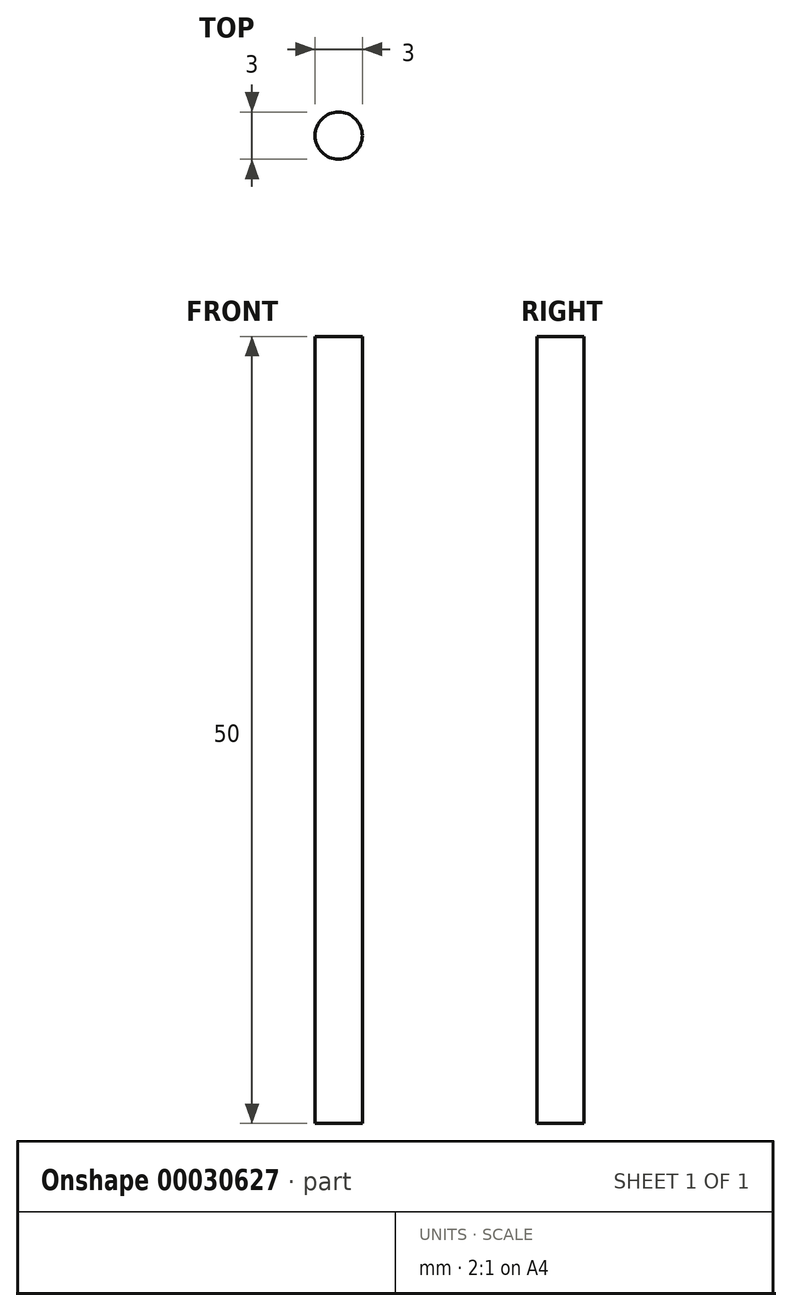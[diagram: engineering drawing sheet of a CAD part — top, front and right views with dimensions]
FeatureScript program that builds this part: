
annotation { "Feature Type Name" : "Feature", "Feature Type Description" : "" }
export const myFeature = defineFeature(function(context is Context, id is Id, definition is map)
    precondition{}
    {
        {
            var Q0;
            Q0=qCreatedBy(makeId("Top.planeOp"),FACE);
            var sketch = newSketch(context, id + "F0", { "sketchPlane" : qUnion([Q0])});
            skCircle(sketch, "E0", {"center": v(0, 0) * mm, "radius": 1.5 * mm});
            skSolve(sketch);
        }
        {
            var Q0;
            Q0 = qSketchRegion(id + "F0", true);
            extrude(context, id + "F1", {"entities" : qUnion([Q0]), "endBound" : BoundingType.SYMMETRIC, "depth" : 50 * mm});
        }
    });
